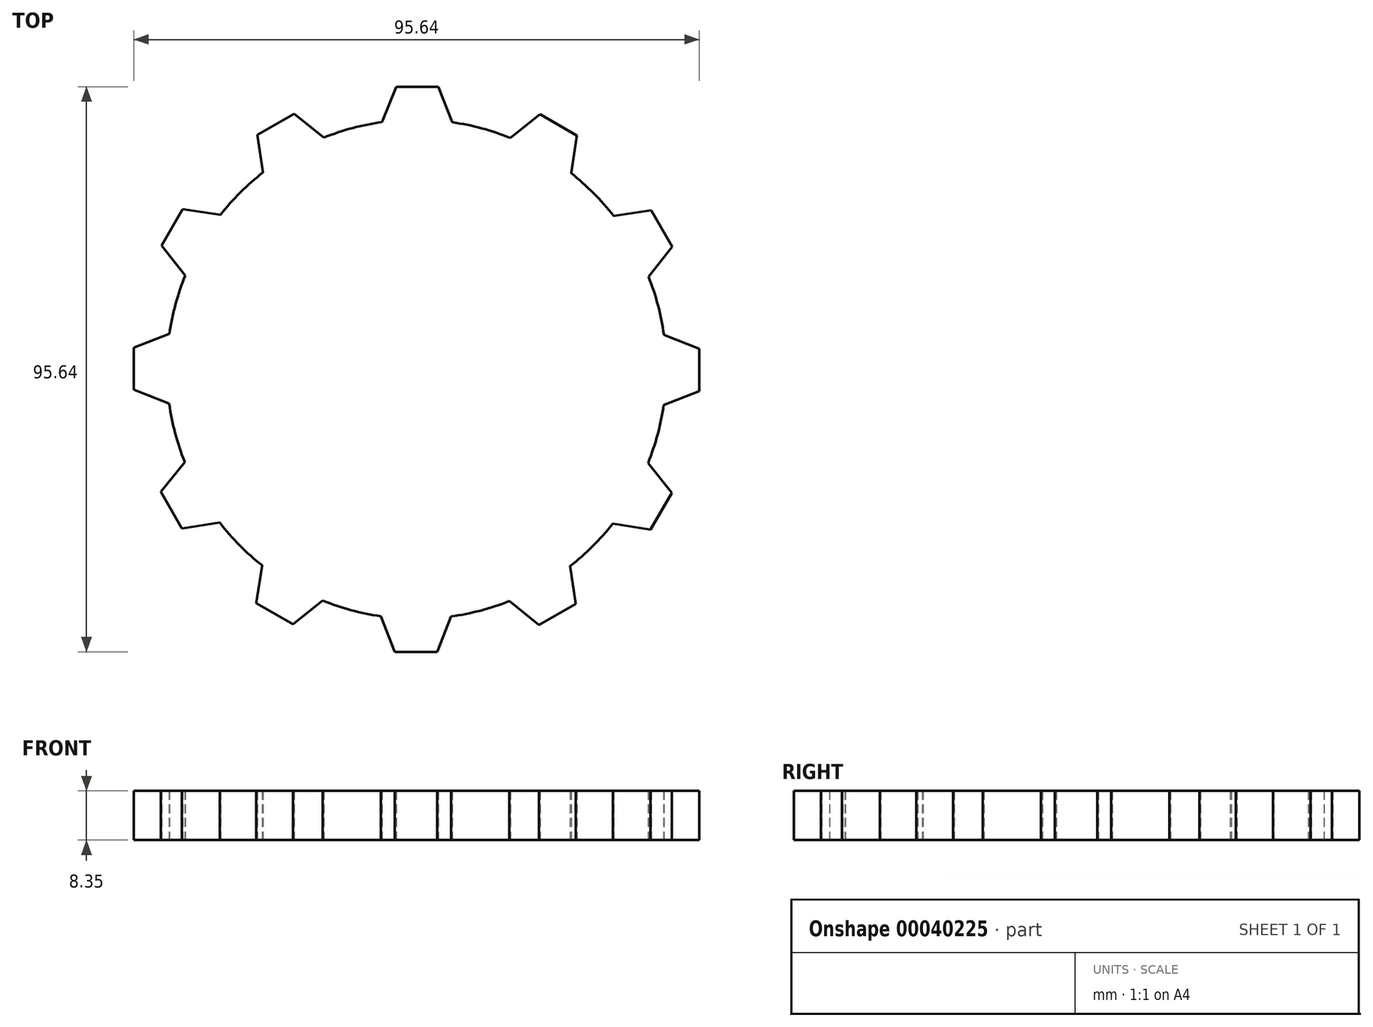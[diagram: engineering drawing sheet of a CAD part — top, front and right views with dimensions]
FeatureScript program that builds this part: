
annotation { "Feature Type Name" : "Feature", "Feature Type Description" : "" }
export const myFeature = defineFeature(function(context is Context, id is Id, definition is map)
    precondition{}
    {
        {
            var Q0;
            Q0=qCreatedBy(makeId("Top.planeOp"),FACE);
            var sketch = newSketch(context, id + "F0", { "sketchPlane" : qUnion([Q0])});
            skArc(sketch, "E0", {"start": v(-5.82, 41.83) * mm, "mid": v(-10.82, 40.82) * mm, "end": v(-15.67, 39.22) * mm});
            skLineSegment(sketch, "E1", {"start": v(-5.82, 41.83) * mm, "end": v(-3.47, 47.82) * mm});
            skLineSegment(sketch, "E2", {"start": v(-3.47, 47.82) * mm, "end": v(3.69, 47.82) * mm});
            skLineSegment(sketch, "E3", {"start": v(3.69, 47.82) * mm, "end": v(6.04, 41.8) * mm});
            skLineSegment(sketch, "E4.1.0", {"start": v(-25.96, 33.32) * mm, "end": v(-26.91, 39.68) * mm});
            skLineSegment(sketch, "E4.1.1", {"start": v(-26.91, 39.68) * mm, "end": v(-20.72, 43.26) * mm});
            skLineSegment(sketch, "E4.1.2", {"start": v(-20.72, 43.26) * mm, "end": v(-15.67, 39.22) * mm});
            skLineSegment(sketch, "E4.2.0", {"start": v(-39.14, 15.87) * mm, "end": v(-43.15, 20.9) * mm});
            skLineSegment(sketch, "E4.2.1", {"start": v(-43.15, 20.9) * mm, "end": v(-39.57, 27.1) * mm});
            skLineSegment(sketch, "E4.2.2", {"start": v(-39.57, 27.1) * mm, "end": v(-33.18, 26.13) * mm});
            skLineSegment(sketch, "E4.3.0", {"start": v(-41.83, -5.82) * mm, "end": v(-47.82, -3.47) * mm});
            skLineSegment(sketch, "E4.3.1", {"start": v(-47.82, -3.47) * mm, "end": v(-47.82, 3.69) * mm});
            skLineSegment(sketch, "E4.3.2", {"start": v(-47.82, 3.69) * mm, "end": v(-41.8, 6.04) * mm});
            skLineSegment(sketch, "E4.4.0", {"start": v(-33.32, -25.96) * mm, "end": v(-39.68, -26.91) * mm});
            skLineSegment(sketch, "E4.4.1", {"start": v(-39.68, -26.91) * mm, "end": v(-43.26, -20.72) * mm});
            skLineSegment(sketch, "E4.4.2", {"start": v(-43.26, -20.72) * mm, "end": v(-39.22, -15.67) * mm});
            skLineSegment(sketch, "E4.5.0", {"start": v(-15.87, -39.14) * mm, "end": v(-20.9, -43.15) * mm});
            skLineSegment(sketch, "E4.5.1", {"start": v(-20.9, -43.15) * mm, "end": v(-27.1, -39.57) * mm});
            skLineSegment(sketch, "E4.5.2", {"start": v(-27.1, -39.57) * mm, "end": v(-26.13, -33.18) * mm});
            skLineSegment(sketch, "E4.6.0", {"start": v(5.82, -41.83) * mm, "end": v(3.47, -47.82) * mm});
            skLineSegment(sketch, "E4.6.1", {"start": v(3.47, -47.82) * mm, "end": v(-3.69, -47.82) * mm});
            skLineSegment(sketch, "E4.6.2", {"start": v(-3.69, -47.82) * mm, "end": v(-6.04, -41.8) * mm});
            skLineSegment(sketch, "E4.7.0", {"start": v(25.96, -33.32) * mm, "end": v(26.91, -39.68) * mm});
            skLineSegment(sketch, "E4.7.1", {"start": v(26.91, -39.68) * mm, "end": v(20.72, -43.26) * mm});
            skLineSegment(sketch, "E4.7.2", {"start": v(20.72, -43.26) * mm, "end": v(15.67, -39.22) * mm});
            skLineSegment(sketch, "E4.8.0", {"start": v(39.14, -15.87) * mm, "end": v(43.15, -20.9) * mm});
            skLineSegment(sketch, "E4.8.1", {"start": v(43.15, -20.9) * mm, "end": v(39.57, -27.1) * mm});
            skLineSegment(sketch, "E4.8.2", {"start": v(39.57, -27.1) * mm, "end": v(33.18, -26.13) * mm});
            skLineSegment(sketch, "E4.9.0", {"start": v(41.83, 5.82) * mm, "end": v(47.82, 3.47) * mm});
            skLineSegment(sketch, "E4.9.1", {"start": v(47.82, 3.47) * mm, "end": v(47.82, -3.69) * mm});
            skLineSegment(sketch, "E4.9.2", {"start": v(47.82, -3.69) * mm, "end": v(41.8, -6.04) * mm});
            skLineSegment(sketch, "E4.10.0", {"start": v(33.32, 25.96) * mm, "end": v(39.68, 26.91) * mm});
            skLineSegment(sketch, "E4.10.1", {"start": v(39.68, 26.91) * mm, "end": v(43.26, 20.72) * mm});
            skLineSegment(sketch, "E4.10.2", {"start": v(43.26, 20.72) * mm, "end": v(39.22, 15.67) * mm});
            skLineSegment(sketch, "E4.11.0", {"start": v(15.87, 39.14) * mm, "end": v(20.9, 43.15) * mm});
            skLineSegment(sketch, "E4.11.1", {"start": v(20.9, 43.15) * mm, "end": v(27.1, 39.57) * mm});
            skLineSegment(sketch, "E4.11.2", {"start": v(27.1, 39.57) * mm, "end": v(26.13, 33.18) * mm});
            skArc(sketch, "E5.trimOffspring", {"start": v(-25.96, 33.32) * mm, "mid": v(-29.79, 29.94) * mm, "end": v(-33.18, 26.13) * mm});
            skArc(sketch, "E6.trimOffspring", {"start": v(-39.14, 15.87) * mm, "mid": v(-40.77, 11.04) * mm, "end": v(-41.8, 6.04) * mm});
            skArc(sketch, "E7.trimOffspring", {"start": v(-41.83, -5.82) * mm, "mid": v(-40.82, -10.82) * mm, "end": v(-39.22, -15.67) * mm});
            skArc(sketch, "E8.trimOffspring", {"start": v(-33.32, -25.96) * mm, "mid": v(-29.94, -29.79) * mm, "end": v(-26.13, -33.18) * mm});
            skArc(sketch, "E9.trimOffspring", {"start": v(-15.87, -39.14) * mm, "mid": v(-11.04, -40.77) * mm, "end": v(-6.04, -41.8) * mm});
            skArc(sketch, "E10.trimOffspring", {"start": v(5.82, -41.83) * mm, "mid": v(10.82, -40.82) * mm, "end": v(15.67, -39.22) * mm});
            skArc(sketch, "E11.trimOffspring", {"start": v(25.96, -33.32) * mm, "mid": v(29.79, -29.94) * mm, "end": v(33.18, -26.13) * mm});
            skArc(sketch, "E12.trimOffspring", {"start": v(39.14, -15.87) * mm, "mid": v(40.77, -11.04) * mm, "end": v(41.8, -6.04) * mm});
            skArc(sketch, "E13.trimOffspring", {"start": v(33.32, 25.96) * mm, "mid": v(29.94, 29.79) * mm, "end": v(26.13, 33.18) * mm});
            skArc(sketch, "E14.trimOffspring", {"start": v(15.87, 39.14) * mm, "mid": v(11.04, 40.77) * mm, "end": v(6.04, 41.8) * mm});
            skArc(sketch, "E15.trimOffspring", {"start": v(41.83, 5.82) * mm, "mid": v(40.82, 10.82) * mm, "end": v(39.22, 15.67) * mm});
            skSolve(sketch);
        }
        {
            var Q0;
            Q0 = qSketchRegion(id + "F0", true);
            extrude(context, id + "F1", {"entities" : qUnion([Q0]), "depth" : 8.35 * mm});
        }
    });
